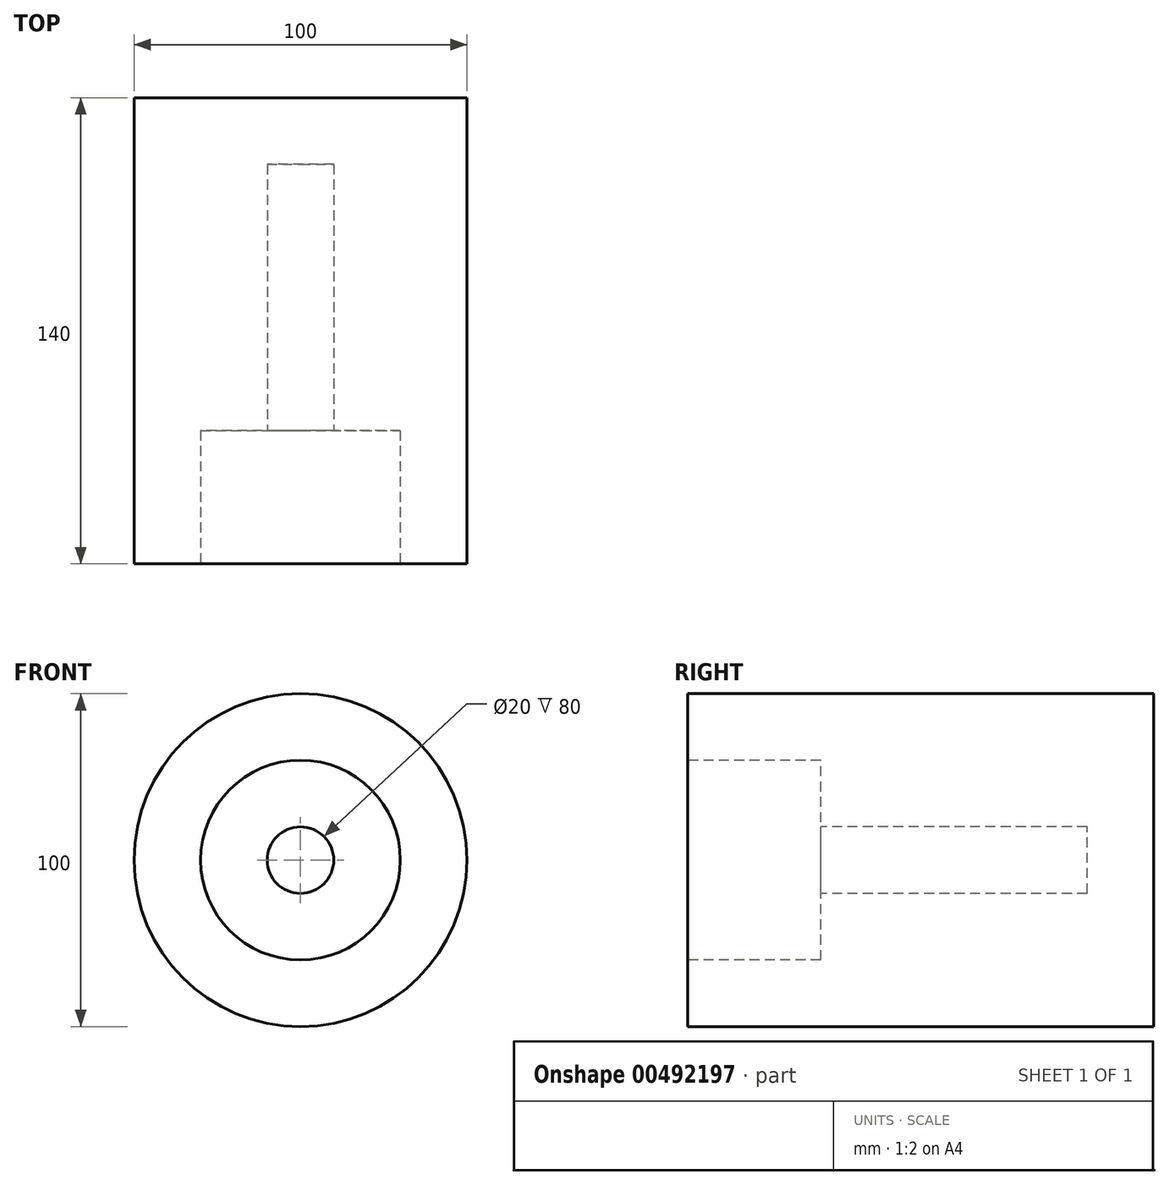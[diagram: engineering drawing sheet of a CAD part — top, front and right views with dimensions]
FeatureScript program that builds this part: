
annotation { "Feature Type Name" : "Feature", "Feature Type Description" : "" }
export const myFeature = defineFeature(function(context is Context, id is Id, definition is map)
    precondition{}
    {
        {
            var Q0;
            Q0=qCreatedBy(makeId("Front.planeOp"),FACE);
            var sketch = newSketch(context, id + "F0", { "sketchPlane" : qUnion([Q0])});
            skCircle(sketch, "E0", {"center": v(0, 0) * mm, "radius": 50 * mm});
            skSolve(sketch);
        }
        {
            var Q0;
            Q0 = qSketchRegion(id + "F0", true);
            extrude(context, id + "F1", {"entities" : qUnion([Q0]), "endBound" : BoundingType.SYMMETRIC, "depth" : 140 * mm, "offsetDistance" : 25 * mm});
        }
        {
            var Q0;
            Q0=makeQuery(id+"F1.opExtrude","CAP_FACE",FACE,{"disambiguationData":[OSD([sQuery(id+"F0.wireOp",EDGE,"E0")])],"isStart":false});
            var sketch = newSketch(context, id + "F2", { "sketchPlane" : qUnion([Q0])});
            skCircle(sketch, "E1", {"center": v(0, 0) * mm, "radius": 30 * mm});
            skSolve(sketch);
        }
        {
            var Q0;
            Q0 = qSketchRegion(id + "F2", true);
            extrude(context, id + "F3", {"entities" : qUnion([Q0]), "operationType" : NewBodyOperationType.REMOVE, "oppositeDirection" : true, "depth" : 40 * mm, "offsetDistance" : 25 * mm});
        }
        {
            var Q0;
            Q0=makeQuery(id+"F3.boolean.opBoolean","COPY",FACE,{"derivedFrom":makeQuery(id+"F3.opExtrude","CAP_FACE",FACE,{"disambiguationData":[OSD([sQuery(id+"F2.wireOp",EDGE,"E1")])],"isStart":false})});
            var sketch = newSketch(context, id + "F4", { "sketchPlane" : qUnion([Q0])});
            skCircle(sketch, "E2", {"center": v(0, 0) * mm, "radius": 10 * mm});
            skSolve(sketch);
        }
        {
            var Q0;
            Q0 = qSketchRegion(id + "F4", true);
            extrude(context, id + "F5", {"entities" : qUnion([Q0]), "operationType" : NewBodyOperationType.REMOVE, "oppositeDirection" : true, "depth" : (120 - 40) * mm, "offsetDistance" : 25 * mm});
        }
    });
